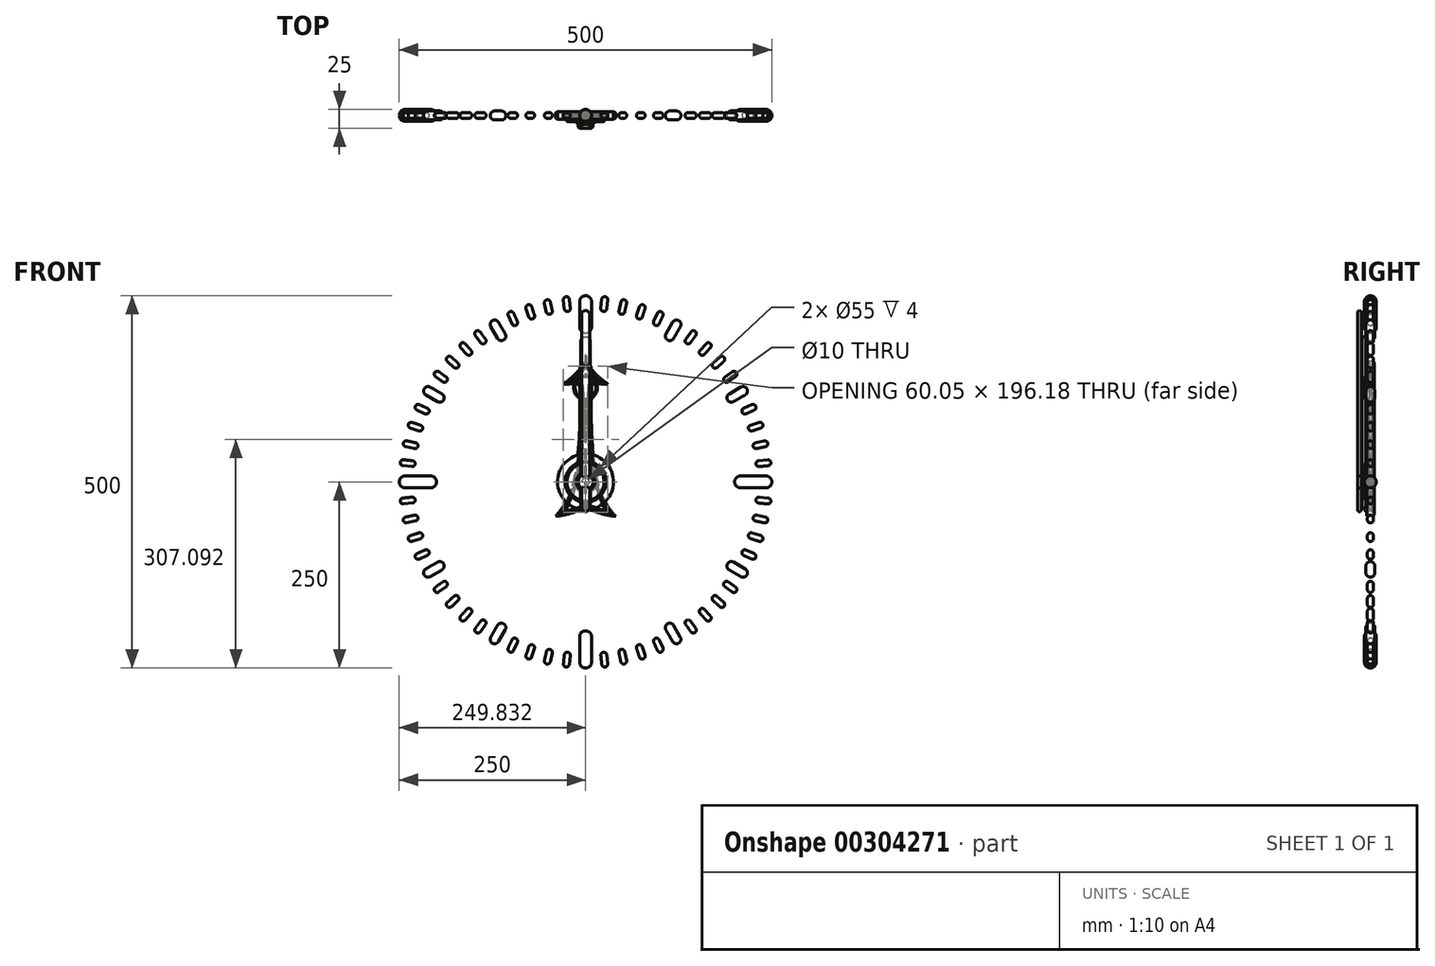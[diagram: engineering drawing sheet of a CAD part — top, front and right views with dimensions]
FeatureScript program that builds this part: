
annotation { "Feature Type Name" : "Feature", "Feature Type Description" : "" }
export const myFeature = defineFeature(function(context is Context, id is Id, definition is map)
    precondition{}
    {
        {
            var Q0;
            Q0=qCreatedBy(makeId("Top.planeOp"),FACE);
            cPlane(context, id + "F0", {"entities" : qUnion([Q0]), "cplaneType" : CPlaneType.OFFSET, "offset" : 250 * mm, "width" : 150 * mm, "height" : 150 * mm});
        }
        {
            var Q0;
            Q0=qCreatedBy(id+"F0.planeOp",FACE);
            var sketch = newSketch(context, id + "F1", { "sketchPlane" : qUnion([Q0])});
            skCircle(sketch, "E0", {"center": v(0, 0) * mm, "radius": 8 * mm});
            skSolve(sketch);
        }
        {
            var Q0;
            Q0 = qSketchRegion(id + "F1", true);
            extrude(context, id + "F2", {"entities" : qUnion([Q0]), "oppositeDirection" : true, "depth" : 50 * mm});
        }
        {
            var Q0;
            Q0=makeQuery(id+"F2.opExtrude","CAP_EDGE",EDGE,{"disambiguationData":[OSD([sQuery(id+"F1.wireOp",EDGE,"E0")])],"isStart":false});
            var Q1;
            Q1=makeQuery(id+"F2.opExtrude","CAP_EDGE",EDGE,{"disambiguationData":[OSD([sQuery(id+"F1.wireOp",EDGE,"E0")])],"isStart":true});
            fillet(context, id + "F3", {"entities" : qUnion([Q0, Q1]), "radius" : 8 * mm, "tangentPropagation" : true, "allowEdgeOverflow" : false});
        }
        {
            var Q0;
            Q0=qCreatedBy(makeId("Top.planeOp"),FACE);
            var sketch = newSketch(context, id + "F4", { "sketchPlane" : qUnion([Q0])});
            skLineSegment(sketch, "E1", {"start": v(0, 0) * mm, "end": v(0, -158.72) * mm});
            skSolve(sketch);
        }
        {
            var Q0;
            Q0=makeQuery(id+"F2.opExtrude","SWEPT_BODY",BODY,{"disambiguationData":[OSD([sQuery(id+"F1.wireOp",EDGE,"E0")])]});
            var Q1;
            Q1=sQuery(id+"F4.wireOp",EDGE,"E1");
            circularPattern(context, id + "F5", {"entities" : qUnion([Q0]), "axis" : qUnion([Q1]), "angle" : 360 * degree, "instanceCount" : 4, "equalSpace" : true});
        }
        {
            var Q0;
            Q0=qCreatedBy(id+"F0.planeOp",FACE);
            var sketch = newSketch(context, id + "F6", { "sketchPlane" : qUnion([Q0])});
            skCircle(sketch, "E2", {"center": v(0, 0) * mm, "radius": 6 * mm});
            skSolve(sketch);
        }
        {
            var Q0;
            Q0 = qSketchRegion(id + "F6", true);
            extrude(context, id + "F7", {"entities" : qUnion([Q0]), "oppositeDirection" : true, "depth" : 30 * mm});
        }
        {
            var Q0;
            Q0=makeQuery(id+"F7.opExtrude","CAP_EDGE",EDGE,{"disambiguationData":[OSD([sQuery(id+"F6.wireOp",EDGE,"E2")])],"isStart":true});
            var Q1;
            Q1=makeQuery(id+"F7.opExtrude","CAP_EDGE",EDGE,{"disambiguationData":[OSD([sQuery(id+"F6.wireOp",EDGE,"E2")])],"isStart":false});
            fillet(context, id + "F8", {"entities" : qUnion([Q0, Q1]), "radius" : 6 * mm, "tangentPropagation" : true, "allowEdgeOverflow" : false});
        }
        {
            var Q0;
            Q0=makeQuery(id+"F7.opExtrude","SWEPT_BODY",BODY,{"disambiguationData":[OSD([sQuery(id+"F6.wireOp",EDGE,"E2")])]});
            var Q1;
            Q1=sQuery(id+"F4.wireOp",EDGE,"E1");
            transform(context, id + "F9", {"entities" : qUnion([Q0]), "transformType" : TransformType.ROTATION, "transformAxis" : qUnion([Q1]), "angle" : 30 * degree, "oppositeDirection" : true, "makeCopy" : true});
        }
        {
            var Q0;
            Q0=makeQuery(id+"F7.opExtrude","SWEPT_BODY",BODY,{"disambiguationData":[OSD([sQuery(id+"F6.wireOp",EDGE,"E2")])]});
            var Q1;
            Q1=sQuery(id+"F4.wireOp",EDGE,"E1");
            transform(context, id + "F10", {"entities" : qUnion([Q0]), "transformType" : TransformType.ROTATION, "transformAxis" : qUnion([Q1]), "angle" : 60 * degree, "oppositeDirection" : true, "makeCopy" : false});
        }
        {
            var Q0;
            Q0=makeQuery(id+"F9.opPattern","COPY",BODY,{"derivedFrom":makeQuery(id+"F7.opExtrude","SWEPT_BODY",BODY,{"disambiguationData":[OSD([sQuery(id+"F6.wireOp",EDGE,"E2")])]}),"instanceName":"1"});
            var Q1;
            Q1=makeQuery(id+"F7.opExtrude","SWEPT_BODY",BODY,{"disambiguationData":[OSD([sQuery(id+"F6.wireOp",EDGE,"E2")])]});
            var Q2;
            Q2=sQuery(id+"F4.wireOp",EDGE,"E1");
            circularPattern(context, id + "F11", {"entities" : qUnion([Q0, Q1]), "axis" : qUnion([Q2]), "angle" : 360 * degree, "instanceCount" : 4, "equalSpace" : true});
        }
        {
            var Q0;
            Q0=qCreatedBy(id+"F0.planeOp",FACE);
            var sketch = newSketch(context, id + "F12", { "sketchPlane" : qUnion([Q0])});
            skCircle(sketch, "E3", {"center": v(0, 0) * mm, "radius": 4 * mm});
            skSolve(sketch);
        }
        {
            var Q0;
            Q0 = qSketchRegion(id + "F12", true);
            extrude(context, id + "F13", {"entities" : qUnion([Q0]), "oppositeDirection" : true, "depth" : 20 * mm});
        }
        {
            var Q0;
            Q0=makeQuery(id+"F13.opExtrude","CAP_EDGE",EDGE,{"disambiguationData":[OSD([sQuery(id+"F12.wireOp",EDGE,"E3")])],"isStart":false});
            var Q1;
            Q1=makeQuery(id+"F13.opExtrude","CAP_EDGE",EDGE,{"disambiguationData":[OSD([sQuery(id+"F12.wireOp",EDGE,"E3")])],"isStart":true});
            fillet(context, id + "F14", {"entities" : qUnion([Q0, Q1]), "radius" : 4 * mm, "tangentPropagation" : true, "allowEdgeOverflow" : false});
        }
        {
            var Q0;
            Q0=makeQuery(id+"F13.opExtrude","SWEPT_BODY",BODY,{"disambiguationData":[OSD([sQuery(id+"F12.wireOp",EDGE,"E3")])]});
            var Q1;
            Q1=sQuery(id+"F4.wireOp",EDGE,"E1");
            transform(context, id + "F15", {"entities" : qUnion([Q0]), "transformType" : TransformType.ROTATION, "transformAxis" : qUnion([Q1]), "angle" : 6 * degree, "oppositeDirection" : true, "makeCopy" : true});
        }
        {
            var Q0;
            Q0=makeQuery(id+"F13.opExtrude","SWEPT_BODY",BODY,{"disambiguationData":[OSD([sQuery(id+"F12.wireOp",EDGE,"E3")])]});
            var Q1;
            Q1=sQuery(id+"F4.wireOp",EDGE,"E1");
            transform(context, id + "F16", {"entities" : qUnion([Q0]), "transformType" : TransformType.ROTATION, "transformAxis" : qUnion([Q1]), "angle" : 12 * degree, "oppositeDirection" : true, "makeCopy" : true});
        }
        {
            var Q0;
            Q0=makeQuery(id+"F13.opExtrude","SWEPT_BODY",BODY,{"disambiguationData":[OSD([sQuery(id+"F12.wireOp",EDGE,"E3")])]});
            var Q1;
            Q1=sQuery(id+"F4.wireOp",EDGE,"E1");
            transform(context, id + "F17", {"entities" : qUnion([Q0]), "transformType" : TransformType.ROTATION, "transformAxis" : qUnion([Q1]), "angle" : 18 * degree, "oppositeDirection" : true, "makeCopy" : true});
        }
        {
            var Q0;
            Q0=makeQuery(id+"F13.opExtrude","SWEPT_BODY",BODY,{"disambiguationData":[OSD([sQuery(id+"F12.wireOp",EDGE,"E3")])]});
            var Q1;
            Q1=sQuery(id+"F4.wireOp",EDGE,"E1");
            transform(context, id + "F18", {"entities" : qUnion([Q0]), "transformType" : TransformType.ROTATION, "transformAxis" : qUnion([Q1]), "angle" : 24 * degree, "oppositeDirection" : true, "makeCopy" : false});
        }
        {
            var Q0;
            Q0=makeQuery(id+"F15.opPattern","COPY",BODY,{"derivedFrom":makeQuery(id+"F13.opExtrude","SWEPT_BODY",BODY,{"disambiguationData":[OSD([sQuery(id+"F12.wireOp",EDGE,"E3")])]}),"instanceName":"1"});
            var Q1;
            Q1=makeQuery(id+"F16.opPattern","COPY",BODY,{"derivedFrom":makeQuery(id+"F13.opExtrude","SWEPT_BODY",BODY,{"disambiguationData":[OSD([sQuery(id+"F12.wireOp",EDGE,"E3")])]}),"instanceName":"1"});
            var Q2;
            Q2=makeQuery(id+"F17.opPattern","COPY",BODY,{"derivedFrom":makeQuery(id+"F13.opExtrude","SWEPT_BODY",BODY,{"disambiguationData":[OSD([sQuery(id+"F12.wireOp",EDGE,"E3")])]}),"instanceName":"1"});
            var Q3;
            Q3=makeQuery(id+"F13.opExtrude","SWEPT_BODY",BODY,{"disambiguationData":[OSD([sQuery(id+"F12.wireOp",EDGE,"E3")])]});
            var Q4;
            Q4=sQuery(id+"F4.wireOp",EDGE,"E1");
            circularPattern(context, id + "F19", {"entities" : qUnion([Q0, Q1, Q2, Q3]), "axis" : qUnion([Q4]), "angle" : 360 * degree, "instanceCount" : 12, "equalSpace" : true});
        }
        {
            var Q0;
            Q0=qCreatedBy(makeId("Front.planeOp"),FACE);
            var sketch = newSketch(context, id + "F20", { "sketchPlane" : qUnion([Q0])});
            skCircle(sketch, "E4", {"center": v(0, 0) * mm, "radius": 15 * mm});
            skLineSegment(sketch, "E5.bottom", {"start": v(7.5, 160) * mm, "end": v(-7.5, 160) * mm});
            skLineSegment(sketch, "E5.top", {"start": v(7.5, -30) * mm, "end": v(-7.5, -30) * mm});
            skLineSegment(sketch, "E5.left", {"start": v(7.5, 160) * mm, "end": v(7.5, -30) * mm});
            skLineSegment(sketch, "E5.right", {"start": v(-7.5, 160) * mm, "end": v(-7.5, -30) * mm});
            skPoint(sketch, "E5.middle", {"position": v(0, 65) * mm});
            skSolve(sketch);
        }
        {
            var Q0;
            Q0 = qSketchRegion(id + "F20", true);
            extrude(context, id + "F21", {"entities" : qUnion([Q0]), "depth" : 5 * mm});
        }
        {
            var Q0;
            Q0=makeQuery(id+"F21.opExtrude","CAP_FACE",FACE,{"disambiguationData":[OSD([sQuery(id+"F20.wireOp",EDGE,"E4"),sQuery(id+"F20.wireOp",EDGE,"E5.bottom"),sQuery(id+"F20.wireOp",EDGE,"E5.top"),sQuery(id+"F20.wireOp",EDGE,"E5.left"),sQuery(id+"F20.wireOp",EDGE,"E5.right")])],"isStart":false});
            cPlane(context, id + "F22", {"entities" : qUnion([Q0]), "cplaneType" : CPlaneType.OFFSET, "offset" : 1 * mm, "width" : 150 * mm, "height" : 150 * mm});
        }
        {
            var Q0;
            Q0=qCreatedBy(id+"F22.planeOp",FACE);
            var sketch = newSketch(context, id + "F23", { "sketchPlane" : qUnion([Q0])});
            skCircle(sketch, "E6", {"center": v(0, 0) * mm, "radius": 12.5 * mm});
            skLineSegment(sketch, "E7.bottom", {"start": v(6.5, -35) * mm, "end": v(-6.5, -35) * mm});
            skLineSegment(sketch, "E7.top", {"start": v(6.5, 195) * mm, "end": v(-6.5, 195) * mm});
            skLineSegment(sketch, "E7.left", {"start": v(6.5, -35) * mm, "end": v(6.5, 195) * mm});
            skLineSegment(sketch, "E7.right", {"start": v(-6.5, -35) * mm, "end": v(-6.5, 195) * mm});
            skPoint(sketch, "E7.middle", {"position": v(0, 80) * mm});
            skSolve(sketch);
        }
        {
            var Q0;
            Q0 = qSketchRegion(id + "F23", true);
            extrude(context, id + "F24", {"entities" : qUnion([Q0]), "depth" : 5 * mm});
        }
        {
            var Q0;
            Q0=makeQuery(id+"F24.opExtrude","CAP_FACE",FACE,{"disambiguationData":[OSD([sQuery(id+"F23.wireOp",EDGE,"E6"),sQuery(id+"F23.wireOp",EDGE,"E7.bottom"),sQuery(id+"F23.wireOp",EDGE,"E7.top"),sQuery(id+"F23.wireOp",EDGE,"E7.left"),sQuery(id+"F23.wireOp",EDGE,"E7.right")])],"isStart":false});
            cPlane(context, id + "F25", {"entities" : qUnion([Q0]), "cplaneType" : CPlaneType.OFFSET, "offset" : 1 * mm, "width" : 150 * mm, "height" : 150 * mm});
        }
        {
            var Q0;
            Q0=qCreatedBy(id+"F25.planeOp",FACE);
            var sketch = newSketch(context, id + "F26", { "sketchPlane" : qUnion([Q0])});
            skCircle(sketch, "E8", {"center": v(0, 0) * mm, "radius": 10 * mm});
            skLineSegment(sketch, "E9.bottom", {"start": v(5.5, -40) * mm, "end": v(-5.5, -40) * mm});
            skLineSegment(sketch, "E9.top", {"start": v(5.5, 230) * mm, "end": v(-5.5, 230) * mm});
            skLineSegment(sketch, "E9.left", {"start": v(5.5, -40) * mm, "end": v(5.5, 230) * mm});
            skLineSegment(sketch, "E9.right", {"start": v(-5.5, -40) * mm, "end": v(-5.5, 230) * mm});
            skPoint(sketch, "E9.middle", {"position": v(0, 95) * mm});
            skSolve(sketch);
        }
        {
            var Q0;
            Q0 = qSketchRegion(id + "F26", true);
            extrude(context, id + "F27", {"entities" : qUnion([Q0]), "depth" : 5 * mm});
        }
        {
            var Q0;
            Q0=qCreatedBy(makeId("Front.planeOp"),FACE);
            var sketch = newSketch(context, id + "F28", { "sketchPlane" : qUnion([Q0])});
            skCircle(sketch, "E10", {"center": v(0, 0) * mm, "radius": 37.5 * mm});
            skCircle(sketch, "E11", {"center": v(0, 0) * mm, "radius": 5 * mm});
            skSolve(sketch);
        }
        {
            var Q0;
            Q0 = qSketchRegion(id + "F28", true);
            extrude(context, id + "F29", {"entities" : qUnion([Q0]), "depth" : 10 * mm, "symmetric" : true});
        }
        {
            var Q0;
            Q0=makeQuery(id+"F29.opExtrude","CAP_FACE",FACE,{"disambiguationData":[OSD([sQuery(id+"F28.wireOp",EDGE,"E10"),sQuery(id+"F28.wireOp",EDGE,"E11")])],"isStart":false});
            var sketch = newSketch(context, id + "F30", { "sketchPlane" : qUnion([Q0])});
            skCircle(sketch, "E12", {"center": v(0, 0) * mm, "radius": 27.5 * mm});
            skCircle(sketch, "E13", {"center": v(0, 0) * mm, "radius": 5 * mm});
            skSolve(sketch);
        }
        {
            var Q0;
            Q0 = qSketchRegion(id + "F30", true);
            extrude(context, id + "F31", {"entities" : qUnion([Q0]), "oppositeDirection" : true, "depth" : 4 * mm});
        }
        {
            var Q0;
            Q0=makeQuery(id+"F31.opExtrude","SWEPT_BODY",BODY,{"disambiguationData":[OSD([sQuery(id+"F30.wireOp",EDGE,"E12"),sQuery(id+"F30.wireOp",EDGE,"E13")])]});
            var Q1;
            Q1=qCreatedBy(makeId("Front.planeOp"),FACE);
            mirror(context, id + "F32", {"entities" : qUnion([Q0]), "mirrorPlane" : qUnion([Q1])});
        }
        {
            var Q0;
            Q0=makeQuery(id+"F31.opExtrude","SWEPT_BODY",BODY,{"disambiguationData":[OSD([sQuery(id+"F30.wireOp",EDGE,"E12"),sQuery(id+"F30.wireOp",EDGE,"E13")])]});
            var Q1;
            Q1=makeQuery(id+"F32.opPattern","COPY",BODY,{"derivedFrom":makeQuery(id+"F31.opExtrude","SWEPT_BODY",BODY,{"disambiguationData":[OSD([sQuery(id+"F30.wireOp",EDGE,"E12"),sQuery(id+"F30.wireOp",EDGE,"E13")])]}),"instanceName":"1"});
            var Q2;
            Q2=makeQuery(id+"F29.opExtrude","SWEPT_BODY",BODY,{"disambiguationData":[OSD([sQuery(id+"F28.wireOp",EDGE,"E10"),sQuery(id+"F28.wireOp",EDGE,"E11")])]});
            booleanBodies(context, id + "F33", {"operationType" : BooleanOperationType.SUBTRACTION, "tools" : qUnion([Q0, Q1]), "targets" : qUnion([Q2])});
        }
        {
            var Q0;
            Q0=qCreatedBy(makeId("Front.planeOp"),FACE);
            var sketch = newSketch(context, id + "F34", { "sketchPlane" : qUnion([Q0])});
            skLineSegment(sketch, "E14", {"start": v(0, 266.38) * mm, "end": v(0, -269.97) * mm, "construction": true});
            skFitSpline(sketch, "E15", {"points": [v(0, -36.62) * mm, v(-40.37, -46.15) * mm], "startDerivative": vector(-46.8, -5.58) * mm, "endDerivative": vector(-74.3, -7.08) * mm});
            skFitSpline(sketch, "E16", {"points": [v(0, 162.63) * mm, v(-29.95, 131.2) * mm], "startDerivative": vector(-29.1, -46) * mm, "endDerivative": vector(-42.46, -30.96) * mm});
            skFitSpline(sketch, "E17", {"points": [v(-29.95, 131.2) * mm, v(-7.93, 120.46) * mm], "startDerivative": vector(71.66, 2.65) * mm, "endDerivative": vector(0.16, -36.44) * mm});
            skFitSpline(sketch, "E18", {"points": [v(-7.93, 120.46) * mm, v(-40.37, -46.15) * mm], "startDerivative": vector(0.4, -90.92) * mm, "endDerivative": vector(-112.63, -107.42) * mm});
            skFitSpline(sketch, "E19.MirrorCS", {"points": [v(0, -36.62) * mm, v(40.37, -46.15) * mm], "startDerivative": vector(46.8, -5.58) * mm, "endDerivative": vector(74.3, -7.08) * mm});
            skFitSpline(sketch, "E20.MirrorCS", {"points": [v(29.95, 131.2) * mm, v(7.93, 120.46) * mm], "startDerivative": vector(-71.66, 2.65) * mm, "endDerivative": vector(-0.16, -36.44) * mm});
            skFitSpline(sketch, "E21.MirrorCS", {"points": [v(7.93, 120.46) * mm, v(40.37, -46.15) * mm], "startDerivative": vector(-0.4, -90.92) * mm, "endDerivative": vector(112.63, -107.42) * mm});
            skFitSpline(sketch, "E22.MirrorCS", {"points": [v(0, 162.63) * mm, v(29.95, 131.2) * mm], "startDerivative": vector(29.1, -46) * mm, "endDerivative": vector(42.46, -30.96) * mm});
            skSolve(sketch);
        }
        {
            var Q0;
            Q0 = qSketchRegion(id + "F34", true);
            extrude(context, id + "F35", {"entities" : qUnion([Q0]), "depth" : 10 * mm, "symmetric" : true});
        }
        {
            var Q0;
            Q0=makeQuery(id+"F35.opExtrude","CAP_FACE",FACE,{"disambiguationData":[OSD([sQuery(id+"F34.wireOp",EDGE,"E15"),sQuery(id+"F34.wireOp",EDGE,"E16"),sQuery(id+"F34.wireOp",EDGE,"E17"),sQuery(id+"F34.wireOp",EDGE,"E18"),sQuery(id+"F34.wireOp",EDGE,"E19.MirrorCS"),sQuery(id+"F34.wireOp",EDGE,"E20.MirrorCS"),sQuery(id+"F34.wireOp",EDGE,"E21.MirrorCS"),sQuery(id+"F34.wireOp",EDGE,"E22.MirrorCS")])],"isStart":false});
            var sketch = newSketch(context, id + "F36", { "sketchPlane" : qUnion([Q0])});
            skFitSpline(sketch, "E23.0", {"points": [v(-30.1, 135.2) * mm, v(-27.12, 135.3) * mm, v(-23.25, 135.47) * mm, v(-19.07, 135.59) * mm, v(-16.36, 135.62) * mm, v(-14.02, 135.56) * mm, v(-11.95, 135.39) * mm, v(-10.36, 135.1) * mm, v(-9.11, 134.7) * mm, v(-8.19, 134.3) * mm, v(-7.29, 133.78) * mm, v(-6.44, 133.1) * mm, v(-5.7, 132.3) * mm, v(-5.12, 131.4) * mm, v(-4.69, 130.5) * mm, v(-4.28, 129.3) * mm, v(-4.03, 127.87) * mm, v(-3.92, 126.2) * mm, v(-3.9, 124.47) * mm, v(-3.92, 122.6) * mm, v(-3.93, 121.21) * mm, v(-3.93, 120.48) * mm]});
            skFitSpline(sketch, "E23.1", {"points": [v(3.38, 160.5) * mm, v(0.92, 156.6) * mm, v(-2.48, 151.6) * mm, v(-6.95, 146) * mm, v(-10.4, 142.2) * mm, v(-14.06, 138.66) * mm, v(-19.38, 134.08) * mm, v(-24.02, 130.57) * mm, v(-27.6, 127.97) * mm]});
            skFitSpline(sketch, "E23.2", {"points": [v(-3.93, 120.48) * mm, v(-3.92, 118.6) * mm, v(-3.87, 114.3) * mm, v(-3.7, 103.68) * mm, v(-3.55, 87.23) * mm, v(-4.03, 64) * mm, v(-5.74, 38.87) * mm, v(-9.24, 13.38) * mm, v(-14.15, -6.89) * mm, v(-19.6, -21.77) * mm, v(-24.53, -32.07) * mm, v(-30.43, -41.31) * mm, v(-35.08, -46.63) * mm, v(-37.6, -49.04) * mm]});
            skFitSpline(sketch, "E23.3", {"points": [v(27.6, 127.97) * mm, v(24.02, 130.57) * mm, v(19.38, 134.08) * mm, v(14.06, 138.66) * mm, v(10.4, 142.2) * mm, v(6.95, 146) * mm, v(2.48, 151.6) * mm, v(-0.92, 156.6) * mm, v(-3.38, 160.5) * mm]});
            skFitSpline(sketch, "E23.4", {"points": [v(-39.78, -42.16) * mm, v(-36.77, -41.88) * mm, v(-31.53, -41.22) * mm, v(-25.59, -40.05) * mm, v(-21.03, -38.8) * mm, v(-17.28, -37.49) * mm, v(-13.73, -36.11) * mm, v(-9.86, -34.74) * mm, v(-5.3, -33.51) * mm, v(-1.6, -32.9) * mm, v(0.47, -32.65) * mm]});
            skFitSpline(sketch, "E23.5", {"points": [v(0.47, -32.65) * mm, v(2.53, -32.9) * mm, v(6.2, -33.5) * mm, v(10.7, -34.71) * mm, v(14.53, -36.08) * mm, v(18.09, -37.45) * mm, v(21.87, -38.77) * mm, v(26.47, -40.04) * mm, v(32.46, -41.21) * mm, v(37.72, -41.88) * mm, v(40.75, -42.16) * mm]});
            skFitSpline(sketch, "E23.6", {"points": [v(37.8, -49.5) * mm, v(35.25, -47.06) * mm, v(30.55, -41.69) * mm, v(24.6, -32.37) * mm, v(19.64, -22) * mm, v(14.17, -7.06) * mm, v(9.25, 13.26) * mm, v(5.74, 38.8) * mm, v(4.04, 63.98) * mm, v(3.55, 87.22) * mm, v(3.7, 103.69) * mm, v(3.87, 114.3) * mm, v(3.92, 118.61) * mm, v(3.93, 120.48) * mm]});
            skFitSpline(sketch, "E23.7", {"points": [v(3.93, 120.48) * mm, v(3.93, 121.21) * mm, v(3.92, 122.6) * mm, v(3.9, 124.47) * mm, v(3.92, 126.2) * mm, v(4.03, 127.87) * mm, v(4.28, 129.3) * mm, v(4.69, 130.5) * mm, v(5.12, 131.4) * mm, v(5.7, 132.3) * mm, v(6.44, 133.1) * mm, v(7.29, 133.78) * mm, v(8.19, 134.3) * mm, v(9.11, 134.7) * mm, v(10.36, 135.1) * mm, v(11.95, 135.39) * mm, v(14.02, 135.56) * mm, v(16.36, 135.62) * mm, v(19.07, 135.59) * mm, v(23.25, 135.47) * mm, v(27.12, 135.3) * mm, v(30.1, 135.2) * mm]});
            skSolve(sketch);
        }
        {
            var Q0;
            Q0 = qSketchRegion(id + "F36", true);
            extrude(context, id + "F37", {"entities" : qUnion([Q0]), "oppositeDirection" : true, "depth" : 3 * mm});
        }
        {
            var Q0;
            Q0=makeQuery(id+"F37.opExtrude","SWEPT_BODY",BODY,{"disambiguationData":[OSD([sQuery(id+"F36.wireOp",EDGE,"cb9f9798-f91a-4ab6-8642-1e6ef36e4919.0.0"),sQuery(id+"F36.wireOp",EDGE,"cb9f9798-f91a-4ab6-8642-1e6ef36e4919.0.1"),sQuery(id+"F36.wireOp",EDGE,"cb9f9798-f91a-4ab6-8642-1e6ef36e4919.0.2"),sQuery(id+"F36.wireOp",EDGE,"cb9f9798-f91a-4ab6-8642-1e6ef36e4919.0.3"),sQuery(id+"F36.wireOp",EDGE,"cb9f9798-f91a-4ab6-8642-1e6ef36e4919.0.4"),sQuery(id+"F36.wireOp",EDGE,"cb9f9798-f91a-4ab6-8642-1e6ef36e4919.0.5"),sQuery(id+"F36.wireOp",EDGE,"cb9f9798-f91a-4ab6-8642-1e6ef36e4919.0.6"),sQuery(id+"F36.wireOp",EDGE,"cb9f9798-f91a-4ab6-8642-1e6ef36e4919.0.7"),sQuery(id+"F36.wireOp",EDGE,"E23.0"),sQuery(id+"F36.wireOp",EDGE,"E23.1"),sQuery(id+"F36.wireOp",EDGE,"E23.2"),sQuery(id+"F36.wireOp",EDGE,"E23.3"),sQuery(id+"F36.wireOp",EDGE,"E23.4"),sQuery(id+"F36.wireOp",EDGE,"E23.5"),sQuery(id+"F36.wireOp",EDGE,"E23.6"),sQuery(id+"F36.wireOp",EDGE,"E23.7")])]});
            var Q1;
            Q1=qCreatedBy(makeId("Front.planeOp"),FACE);
            mirror(context, id + "F38", {"entities" : qUnion([Q0]), "mirrorPlane" : qUnion([Q1])});
        }
        {
            var Q0;
            Q0=makeQuery(id+"F37.opExtrude","SWEPT_BODY",BODY,{"disambiguationData":[OSD([sQuery(id+"F36.wireOp",EDGE,"cb9f9798-f91a-4ab6-8642-1e6ef36e4919.0.0"),sQuery(id+"F36.wireOp",EDGE,"cb9f9798-f91a-4ab6-8642-1e6ef36e4919.0.1"),sQuery(id+"F36.wireOp",EDGE,"cb9f9798-f91a-4ab6-8642-1e6ef36e4919.0.2"),sQuery(id+"F36.wireOp",EDGE,"cb9f9798-f91a-4ab6-8642-1e6ef36e4919.0.3"),sQuery(id+"F36.wireOp",EDGE,"cb9f9798-f91a-4ab6-8642-1e6ef36e4919.0.4"),sQuery(id+"F36.wireOp",EDGE,"cb9f9798-f91a-4ab6-8642-1e6ef36e4919.0.5"),sQuery(id+"F36.wireOp",EDGE,"cb9f9798-f91a-4ab6-8642-1e6ef36e4919.0.6"),sQuery(id+"F36.wireOp",EDGE,"cb9f9798-f91a-4ab6-8642-1e6ef36e4919.0.7"),sQuery(id+"F36.wireOp",EDGE,"E23.0"),sQuery(id+"F36.wireOp",EDGE,"E23.1"),sQuery(id+"F36.wireOp",EDGE,"E23.2"),sQuery(id+"F36.wireOp",EDGE,"E23.3"),sQuery(id+"F36.wireOp",EDGE,"E23.4"),sQuery(id+"F36.wireOp",EDGE,"E23.5"),sQuery(id+"F36.wireOp",EDGE,"E23.6"),sQuery(id+"F36.wireOp",EDGE,"E23.7")])]});
            var Q1;
            Q1=makeQuery(id+"F38.opPattern","COPY",BODY,{"derivedFrom":makeQuery(id+"F37.opExtrude","SWEPT_BODY",BODY,{"disambiguationData":[OSD([sQuery(id+"F36.wireOp",EDGE,"cb9f9798-f91a-4ab6-8642-1e6ef36e4919.0.0"),sQuery(id+"F36.wireOp",EDGE,"cb9f9798-f91a-4ab6-8642-1e6ef36e4919.0.1"),sQuery(id+"F36.wireOp",EDGE,"cb9f9798-f91a-4ab6-8642-1e6ef36e4919.0.2"),sQuery(id+"F36.wireOp",EDGE,"cb9f9798-f91a-4ab6-8642-1e6ef36e4919.0.3"),sQuery(id+"F36.wireOp",EDGE,"cb9f9798-f91a-4ab6-8642-1e6ef36e4919.0.4"),sQuery(id+"F36.wireOp",EDGE,"cb9f9798-f91a-4ab6-8642-1e6ef36e4919.0.5"),sQuery(id+"F36.wireOp",EDGE,"cb9f9798-f91a-4ab6-8642-1e6ef36e4919.0.6"),sQuery(id+"F36.wireOp",EDGE,"cb9f9798-f91a-4ab6-8642-1e6ef36e4919.0.7"),sQuery(id+"F36.wireOp",EDGE,"E23.0"),sQuery(id+"F36.wireOp",EDGE,"E23.1"),sQuery(id+"F36.wireOp",EDGE,"E23.2"),sQuery(id+"F36.wireOp",EDGE,"E23.3"),sQuery(id+"F36.wireOp",EDGE,"E23.4"),sQuery(id+"F36.wireOp",EDGE,"E23.5"),sQuery(id+"F36.wireOp",EDGE,"E23.6"),sQuery(id+"F36.wireOp",EDGE,"E23.7")])]}),"instanceName":"1"});
            var Q2;
            Q2=makeQuery(id+"F35.opExtrude","SWEPT_BODY",BODY,{"disambiguationData":[OSD([sQuery(id+"F34.wireOp",EDGE,"E15"),sQuery(id+"F34.wireOp",EDGE,"E16"),sQuery(id+"F34.wireOp",EDGE,"E17"),sQuery(id+"F34.wireOp",EDGE,"E18"),sQuery(id+"F34.wireOp",EDGE,"E19.MirrorCS"),sQuery(id+"F34.wireOp",EDGE,"E20.MirrorCS"),sQuery(id+"F34.wireOp",EDGE,"E21.MirrorCS"),sQuery(id+"F34.wireOp",EDGE,"E22.MirrorCS")])]});
            booleanBodies(context, id + "F39", {"operationType" : BooleanOperationType.SUBTRACTION, "tools" : qUnion([Q0, Q1]), "targets" : qUnion([Q2])});
        }
        {
            var Q0;
            Q0=makeQuery(id+"F39.opBoolean","COPY",EDGE,{"derivedFrom":makeQuery(id+"F38.opPattern","COPY",EDGE,{"derivedFrom":makeQuery(id+"F37.opExtrude","SWEPT_EDGE",EDGE,{"disambiguationData":[OSD([sQuery(id+"F36.wireOp",EDGE,"E23.4"),sQuery(id+"F36.wireOp",EDGE,"E23.5")])]}),"instanceName":"1"})});
            var Q1;
            Q1=makeQuery(id+"F35.opExtrude","SWEPT_EDGE",EDGE,{"disambiguationData":[OSD([sQuery(id+"F34.wireOp",EDGE,"E15"),sQuery(id+"F34.wireOp",EDGE,"E19.MirrorCS")])]});
            var Q2;
            Q2=makeQuery(id+"F39.opBoolean","COPY",EDGE,{"derivedFrom":makeQuery(id+"F37.opExtrude","SWEPT_EDGE",EDGE,{"disambiguationData":[OSD([sQuery(id+"F36.wireOp",EDGE,"E23.4"),sQuery(id+"F36.wireOp",EDGE,"E23.5")])]})});
            fillet(context, id + "F40", {"entities" : qUnion([Q0, Q1, Q2]), "radius" : 10 * mm, "tangentPropagation" : true, "allowEdgeOverflow" : false});
        }
        {
            var Q0;
            Q0=makeQuery(id+"F39.opBoolean","COPY",EDGE,{"derivedFrom":makeQuery(id+"F37.opExtrude","CAP_EDGE",EDGE,{"disambiguationData":[OSD([sQuery(id+"F36.wireOp",EDGE,"9ae596dd-88c0-4f9c-ab1a-e39f6d769622.5")])],"isStart":true})});
            var Q1;
            Q1=makeQuery(id+"F39.opBoolean","COPY",EDGE,{"derivedFrom":makeQuery(id+"F37.opExtrude","CAP_EDGE",EDGE,{"disambiguationData":[OSD([sQuery(id+"F36.wireOp",EDGE,"9ae596dd-88c0-4f9c-ab1a-e39f6d769622.6")])],"isStart":true})});
            var Q2;
            Q2=makeQuery(id+"F39.opBoolean","COPY",EDGE,{"derivedFrom":makeQuery(id+"F37.opExtrude","CAP_EDGE",EDGE,{"disambiguationData":[OSD([sQuery(id+"F36.wireOp",EDGE,"9ae596dd-88c0-4f9c-ab1a-e39f6d769622.7")])],"isStart":true})});
            var Q3;
            Q3=makeQuery(id+"F39.opBoolean","COPY",EDGE,{"derivedFrom":makeQuery(id+"F37.opExtrude","CAP_EDGE",EDGE,{"disambiguationData":[OSD([sQuery(id+"F36.wireOp",EDGE,"9ae596dd-88c0-4f9c-ab1a-e39f6d769622.3")])],"isStart":true})});
            var Q4;
            Q4=makeQuery(id+"F39.opBoolean","COPY",EDGE,{"derivedFrom":makeQuery(id+"F38.opPattern","COPY",EDGE,{"derivedFrom":makeQuery(id+"F37.opExtrude","CAP_EDGE",EDGE,{"disambiguationData":[OSD([sQuery(id+"F36.wireOp",EDGE,"9ae596dd-88c0-4f9c-ab1a-e39f6d769622.7")])],"isStart":true}),"instanceName":"1"})});
            var Q5;
            Q5=makeQuery(id+"F39.opBoolean","COPY",EDGE,{"derivedFrom":makeQuery(id+"F38.opPattern","COPY",EDGE,{"derivedFrom":makeQuery(id+"F37.opExtrude","CAP_EDGE",EDGE,{"disambiguationData":[OSD([sQuery(id+"F36.wireOp",EDGE,"9ae596dd-88c0-4f9c-ab1a-e39f6d769622.5")])],"isStart":true}),"instanceName":"1"})});
            var Q6;
            Q6=makeQuery(id+"F39.opBoolean","COPY",EDGE,{"derivedFrom":makeQuery(id+"F38.opPattern","COPY",EDGE,{"derivedFrom":makeQuery(id+"F37.opExtrude","CAP_EDGE",EDGE,{"disambiguationData":[OSD([sQuery(id+"F36.wireOp",EDGE,"9ae596dd-88c0-4f9c-ab1a-e39f6d769622.3")])],"isStart":true}),"instanceName":"1"})});
            var Q7;
            Q7=makeQuery(id+"F39.opBoolean","COPY",EDGE,{"derivedFrom":makeQuery(id+"F38.opPattern","COPY",EDGE,{"derivedFrom":makeQuery(id+"F37.opExtrude","CAP_EDGE",EDGE,{"disambiguationData":[OSD([sQuery(id+"F36.wireOp",EDGE,"9ae596dd-88c0-4f9c-ab1a-e39f6d769622.6")])],"isStart":true}),"instanceName":"1"})});
            var Q8;
            Q8=makeQuery(id+"F35.opExtrude","CAP_EDGE",EDGE,{"disambiguationData":[OSD([sQuery(id+"F34.wireOp",EDGE,"E21.MirrorCS")])],"isStart":true});
            var Q9;
            Q9=makeQuery(id+"F35.opExtrude","CAP_EDGE",EDGE,{"disambiguationData":[OSD([sQuery(id+"F34.wireOp",EDGE,"E21.MirrorCS")])],"isStart":false});
            var Q10;
            Q10=makeQuery(id+"F35.opExtrude","CAP_EDGE",EDGE,{"disambiguationData":[OSD([sQuery(id+"F34.wireOp",EDGE,"E18")])],"isStart":true});
            var Q11;
            Q11=makeQuery(id+"F35.opExtrude","CAP_EDGE",EDGE,{"disambiguationData":[OSD([sQuery(id+"F34.wireOp",EDGE,"E18")])],"isStart":false});
            var Q12;
            Q12=makeQuery(id+"F35.opExtrude","CAP_EDGE",EDGE,{"disambiguationData":[OSD([sQuery(id+"F34.wireOp",EDGE,"E15")])],"isStart":true});
            var Q13;
            Q13=makeQuery(id+"F35.opExtrude","CAP_EDGE",EDGE,{"disambiguationData":[OSD([sQuery(id+"F34.wireOp",EDGE,"E19.MirrorCS")])],"isStart":true});
            var Q14;
            Q14=makeQuery(id+"F35.opExtrude","CAP_EDGE",EDGE,{"disambiguationData":[OSD([sQuery(id+"F34.wireOp",EDGE,"E15")])],"isStart":false});
            var Q15;
            Q15=makeQuery(id+"F35.opExtrude","CAP_EDGE",EDGE,{"disambiguationData":[OSD([sQuery(id+"F34.wireOp",EDGE,"E19.MirrorCS")])],"isStart":false});
            var Q16;
            Q16=makeQuery(id+"F35.opExtrude","SWEPT_EDGE",EDGE,{"disambiguationData":[OSD([sQuery(id+"F34.wireOp",EDGE,"E15"),sQuery(id+"F34.wireOp",EDGE,"E19.MirrorCS")])]});
            var Q17;
            Q17=makeQuery(id+"F39.opBoolean","COPY",EDGE,{"derivedFrom":makeQuery(id+"F38.opPattern","COPY",EDGE,{"derivedFrom":makeQuery(id+"F37.opExtrude","SWEPT_EDGE",EDGE,{"disambiguationData":[OSD([sQuery(id+"F36.wireOp",EDGE,"9ae596dd-88c0-4f9c-ab1a-e39f6d769622.6"),sQuery(id+"F36.wireOp",EDGE,"9ae596dd-88c0-4f9c-ab1a-e39f6d769622.7")])]}),"instanceName":"1"})});
            var Q18;
            Q18=makeQuery(id+"F35.opExtrude","CAP_EDGE",EDGE,{"disambiguationData":[OSD([sQuery(id+"F34.wireOp",EDGE,"E16")])],"isStart":true});
            var Q19;
            Q19=makeQuery(id+"F35.opExtrude","CAP_EDGE",EDGE,{"disambiguationData":[OSD([sQuery(id+"F34.wireOp",EDGE,"E22.MirrorCS")])],"isStart":true});
            var Q20;
            Q20=makeQuery(id+"F39.opBoolean","COPY",EDGE,{"derivedFrom":makeQuery(id+"F38.opPattern","COPY",EDGE,{"derivedFrom":makeQuery(id+"F37.opExtrude","CAP_EDGE",EDGE,{"disambiguationData":[OSD([sQuery(id+"F36.wireOp",EDGE,"9ae596dd-88c0-4f9c-ab1a-e39f6d769622.0")])],"isStart":true}),"instanceName":"1"})});
            var Q21;
            Q21=makeQuery(id+"F39.opBoolean","COPY",EDGE,{"derivedFrom":makeQuery(id+"F38.opPattern","COPY",EDGE,{"derivedFrom":makeQuery(id+"F37.opExtrude","CAP_EDGE",EDGE,{"disambiguationData":[OSD([sQuery(id+"F36.wireOp",EDGE,"9ae596dd-88c0-4f9c-ab1a-e39f6d769622.2")])],"isStart":true}),"instanceName":"1"})});
            var Q22;
            Q22=makeQuery(id+"F35.opExtrude","CAP_EDGE",EDGE,{"disambiguationData":[OSD([sQuery(id+"F34.wireOp",EDGE,"E16")])],"isStart":false});
            var Q23;
            Q23=makeQuery(id+"F39.opBoolean","COPY",EDGE,{"derivedFrom":makeQuery(id+"F37.opExtrude","CAP_EDGE",EDGE,{"disambiguationData":[OSD([sQuery(id+"F36.wireOp",EDGE,"9ae596dd-88c0-4f9c-ab1a-e39f6d769622.2")])],"isStart":true})});
            var Q24;
            Q24=makeQuery(id+"F39.opBoolean","COPY",EDGE,{"derivedFrom":makeQuery(id+"F37.opExtrude","CAP_EDGE",EDGE,{"disambiguationData":[OSD([sQuery(id+"F36.wireOp",EDGE,"9ae596dd-88c0-4f9c-ab1a-e39f6d769622.0")])],"isStart":true})});
            var Q25;
            Q25=makeQuery(id+"F35.opExtrude","CAP_EDGE",EDGE,{"disambiguationData":[OSD([sQuery(id+"F34.wireOp",EDGE,"E22.MirrorCS")])],"isStart":false});
            var Q26;
            Q26=makeQuery(id+"F35.opExtrude","CAP_EDGE",EDGE,{"disambiguationData":[OSD([sQuery(id+"F34.wireOp",EDGE,"E17")])],"isStart":false});
            fillet(context, id + "F41", {"entities" : qUnion([Q0, Q1, Q2, Q3, Q4, Q5, Q6, Q7, Q8, Q9, Q10, Q11, Q12, Q13, Q14, Q15, Q16, Q17, Q18, Q19, Q20, Q21, Q22, Q23, Q24, Q25, Q26]), "radius" : 2 * mm, "tangentPropagation" : true, "allowEdgeOverflow" : false});
        }
        {
            var Q0;
            Q0=makeQuery(id+"F39.opBoolean","COPY",EDGE,{"derivedFrom":makeQuery(id+"F37.opExtrude","CAP_EDGE",EDGE,{"disambiguationData":[OSD([sQuery(id+"F36.wireOp",EDGE,"E23.1")])],"isStart":true})});
            var Q1;
            Q1=makeQuery(id+"F39.opBoolean","COPY",EDGE,{"derivedFrom":makeQuery(id+"F37.opExtrude","CAP_EDGE",EDGE,{"disambiguationData":[OSD([sQuery(id+"F36.wireOp",EDGE,"E23.1")])],"isStart":false})});
            var Q2;
            Q2=makeQuery(id+"F39.opBoolean","COPY",EDGE,{"derivedFrom":makeQuery(id+"F37.opExtrude","CAP_EDGE",EDGE,{"disambiguationData":[OSD([sQuery(id+"F36.wireOp",EDGE,"E23.3")])],"isStart":false})});
            var Q3;
            Q3=makeQuery(id+"F39.opBoolean","COPY",EDGE,{"derivedFrom":makeQuery(id+"F37.opExtrude","CAP_EDGE",EDGE,{"disambiguationData":[OSD([sQuery(id+"F36.wireOp",EDGE,"E23.3")])],"isStart":true})});
            var Q4;
            Q4=makeQuery(id+"F39.opBoolean","COPY",EDGE,{"derivedFrom":makeQuery(id+"F37.opExtrude","CAP_EDGE",EDGE,{"disambiguationData":[OSD([sQuery(id+"F36.wireOp",EDGE,"E23.7")])],"isStart":false})});
            var Q5;
            Q5=makeQuery(id+"F39.opBoolean","COPY",EDGE,{"derivedFrom":makeQuery(id+"F37.opExtrude","CAP_EDGE",EDGE,{"disambiguationData":[OSD([sQuery(id+"F36.wireOp",EDGE,"E23.7")])],"isStart":true})});
            var Q6;
            Q6=makeQuery(id+"F39.opBoolean","COPY",EDGE,{"derivedFrom":makeQuery(id+"F37.opExtrude","CAP_EDGE",EDGE,{"disambiguationData":[OSD([sQuery(id+"F36.wireOp",EDGE,"E23.0")])],"isStart":true})});
            var Q7;
            Q7=makeQuery(id+"F39.opBoolean","COPY",EDGE,{"derivedFrom":makeQuery(id+"F37.opExtrude","CAP_EDGE",EDGE,{"disambiguationData":[OSD([sQuery(id+"F36.wireOp",EDGE,"E23.0")])],"isStart":false})});
            var Q8;
            Q8=makeQuery(id+"F39.opBoolean","COPY",EDGE,{"derivedFrom":makeQuery(id+"F37.opExtrude","CAP_EDGE",EDGE,{"disambiguationData":[OSD([sQuery(id+"F36.wireOp",EDGE,"E23.4")])],"isStart":false})});
            var Q9;
            Q9=makeQuery(id+"F39.opBoolean","COPY",EDGE,{"derivedFrom":makeQuery(id+"F37.opExtrude","CAP_EDGE",EDGE,{"disambiguationData":[OSD([sQuery(id+"F36.wireOp",EDGE,"E23.5")])],"isStart":false})});
            var Q10;
            Q10=makeQuery(id+"F39.opBoolean","COPY",EDGE,{"derivedFrom":makeQuery(id+"F37.opExtrude","CAP_EDGE",EDGE,{"disambiguationData":[OSD([sQuery(id+"F36.wireOp",EDGE,"E23.5")])],"isStart":true})});
            var Q11;
            Q11=makeQuery(id+"F39.opBoolean","COPY",EDGE,{"derivedFrom":makeQuery(id+"F37.opExtrude","CAP_EDGE",EDGE,{"disambiguationData":[OSD([sQuery(id+"F36.wireOp",EDGE,"E23.4")])],"isStart":true})});
            var Q12;
            Q12=makeQuery(id+"F39.opBoolean","COPY",EDGE,{"derivedFrom":makeQuery(id+"F38.opPattern","COPY",EDGE,{"derivedFrom":makeQuery(id+"F37.opExtrude","CAP_EDGE",EDGE,{"disambiguationData":[OSD([sQuery(id+"F36.wireOp",EDGE,"E23.3")])],"isStart":false}),"instanceName":"1"})});
            var Q13;
            Q13=makeQuery(id+"F39.opBoolean","COPY",EDGE,{"derivedFrom":makeQuery(id+"F38.opPattern","COPY",EDGE,{"derivedFrom":makeQuery(id+"F37.opExtrude","CAP_EDGE",EDGE,{"disambiguationData":[OSD([sQuery(id+"F36.wireOp",EDGE,"E23.3")])],"isStart":true}),"instanceName":"1"})});
            var Q14;
            Q14=makeQuery(id+"F39.opBoolean","COPY",EDGE,{"derivedFrom":makeQuery(id+"F38.opPattern","COPY",EDGE,{"derivedFrom":makeQuery(id+"F37.opExtrude","CAP_EDGE",EDGE,{"disambiguationData":[OSD([sQuery(id+"F36.wireOp",EDGE,"E23.1")])],"isStart":false}),"instanceName":"1"})});
            var Q15;
            Q15=makeQuery(id+"F39.opBoolean","COPY",EDGE,{"derivedFrom":makeQuery(id+"F38.opPattern","COPY",EDGE,{"derivedFrom":makeQuery(id+"F37.opExtrude","CAP_EDGE",EDGE,{"disambiguationData":[OSD([sQuery(id+"F36.wireOp",EDGE,"E23.1")])],"isStart":true}),"instanceName":"1"})});
            var Q16;
            Q16=makeQuery(id+"F39.opBoolean","COPY",EDGE,{"derivedFrom":makeQuery(id+"F38.opPattern","COPY",EDGE,{"derivedFrom":makeQuery(id+"F37.opExtrude","CAP_EDGE",EDGE,{"disambiguationData":[OSD([sQuery(id+"F36.wireOp",EDGE,"E23.7")])],"isStart":true}),"instanceName":"1"})});
            var Q17;
            Q17=makeQuery(id+"F39.opBoolean","COPY",EDGE,{"derivedFrom":makeQuery(id+"F38.opPattern","COPY",EDGE,{"derivedFrom":makeQuery(id+"F37.opExtrude","CAP_EDGE",EDGE,{"disambiguationData":[OSD([sQuery(id+"F36.wireOp",EDGE,"E23.7")])],"isStart":false}),"instanceName":"1"})});
            var Q18;
            Q18=makeQuery(id+"F39.opBoolean","COPY",EDGE,{"derivedFrom":makeQuery(id+"F38.opPattern","COPY",EDGE,{"derivedFrom":makeQuery(id+"F37.opExtrude","CAP_EDGE",EDGE,{"disambiguationData":[OSD([sQuery(id+"F36.wireOp",EDGE,"E23.0")])],"isStart":false}),"instanceName":"1"})});
            var Q19;
            Q19=makeQuery(id+"F39.opBoolean","COPY",EDGE,{"derivedFrom":makeQuery(id+"F38.opPattern","COPY",EDGE,{"derivedFrom":makeQuery(id+"F37.opExtrude","CAP_EDGE",EDGE,{"disambiguationData":[OSD([sQuery(id+"F36.wireOp",EDGE,"E23.0")])],"isStart":true}),"instanceName":"1"})});
            var Q20;
            Q20=makeQuery(id+"F39.opBoolean","COPY",EDGE,{"derivedFrom":makeQuery(id+"F38.opPattern","COPY",EDGE,{"derivedFrom":makeQuery(id+"F37.opExtrude","CAP_EDGE",EDGE,{"disambiguationData":[OSD([sQuery(id+"F36.wireOp",EDGE,"E23.5")])],"isStart":false}),"instanceName":"1"})});
            var Q21;
            Q21=makeQuery(id+"F39.opBoolean","COPY",EDGE,{"derivedFrom":makeQuery(id+"F38.opPattern","COPY",EDGE,{"derivedFrom":makeQuery(id+"F37.opExtrude","CAP_EDGE",EDGE,{"disambiguationData":[OSD([sQuery(id+"F36.wireOp",EDGE,"E23.5")])],"isStart":true}),"instanceName":"1"})});
            var Q22;
            Q22=makeQuery(id+"F39.opBoolean","COPY",EDGE,{"derivedFrom":makeQuery(id+"F38.opPattern","COPY",EDGE,{"derivedFrom":makeQuery(id+"F37.opExtrude","CAP_EDGE",EDGE,{"disambiguationData":[OSD([sQuery(id+"F36.wireOp",EDGE,"E23.4")])],"isStart":false}),"instanceName":"1"})});
            var Q23;
            Q23=makeQuery(id+"F39.opBoolean","COPY",EDGE,{"derivedFrom":makeQuery(id+"F38.opPattern","COPY",EDGE,{"derivedFrom":makeQuery(id+"F37.opExtrude","CAP_EDGE",EDGE,{"disambiguationData":[OSD([sQuery(id+"F36.wireOp",EDGE,"E23.4")])],"isStart":true}),"instanceName":"1"})});
            fillet(context, id + "F42", {"entities" : qUnion([Q0, Q1, Q2, Q3, Q4, Q5, Q6, Q7, Q8, Q9, Q10, Q11, Q12, Q13, Q14, Q15, Q16, Q17, Q18, Q19, Q20, Q21, Q22, Q23]), "radius" : 1 * mm, "tangentPropagation" : true, "allowEdgeOverflow" : false});
        }
        {
            var Q0;
            Q0=qCreatedBy(id+"F22.planeOp",FACE);
            var sketch = newSketch(context, id + "F43", { "sketchPlane" : qUnion([Q0])});
            skLineSegment(sketch, "E24", {"start": v(0, 310.17) * mm, "end": v(0, -199.61) * mm, "construction": true});
            skCircle(sketch, "E25", {"center": v(0, 0) * mm, "radius": 25 * mm});
            skSolve(sketch);
        }
        {
            var Q0;
            Q0 = qSketchRegion(id + "F43", true);
            extrude(context, id + "F44", {"entities" : qUnion([Q0]), "depth" : 5 * mm, "symmetric" : true});
        }
        {
            var Q0;
            Q0=qCreatedBy(id+"F22.planeOp",FACE);
            var sketch = newSketch(context, id + "F45", { "sketchPlane" : qUnion([Q0])});
            skLineSegment(sketch, "E26", {"start": v(0, 111.2) * mm, "end": v(0, -40) * mm});
            skCircle(sketch, "E27", {"center": v(0, 126.2) * mm, "radius": 15 * mm});
            skLineSegment(sketch, "E28", {"start": v(0, 141.2) * mm, "end": v(0, 170) * mm});
            skSolve(sketch);
        }
        {
            var Q0;
            Q0=sQuery(id+"F45.wireOp",EDGE,"E28");
            var Q1;
            Q1=sQuery(id+"F45.wireOp",VERTEX,"E28.end");
            cPlane(context, id + "F46", {"entities" : qUnion([Q0, Q1]), "cplaneType" : CPlaneType.LINE_POINT, "offset" : 25 * mm, "width" : 150 * mm, "height" : 150 * mm});
        }
        {
            var Q0;
            Q0=qCreatedBy(id+"F46.planeOp",FACE);
            var sketch = newSketch(context, id + "F47", { "sketchPlane" : qUnion([Q0])});
            skCircle(sketch, "E29", {"center": v(0, -6) * mm, "radius": 1 * mm});
            skSolve(sketch);
        }
        {
            var Q0;
            Q0=makeQuery(id+"F47.imprint","IMPRINT",FACE,{"disambiguationData":[TD([[makeQuery(id+"F47.imprint","IMPRINT",EDGE,{"derivedFrom":sQuery(id+"F47.wireOp",EDGE,"E29")}),1.0]])]});
            var Q1;
            Q1=sQuery(id+"F45.wireOp",EDGE,"E28");
            sweep(context, id + "F48", {"profiles" : qUnion([Q0]), "path" : qUnion([Q1])});
        }
        {
            var Q0;
            Q0=sQuery(id+"F45.wireOp",VERTEX,"E26.end");
            var Q1;
            Q1=sQuery(id+"F45.wireOp",EDGE,"E26");
            cPlane(context, id + "F49", {"entities" : qUnion([Q0, Q1]), "cplaneType" : CPlaneType.LINE_POINT, "offset" : 25 * mm, "width" : 150 * mm, "height" : 150 * mm});
        }
        {
            var Q0;
            Q0=qCreatedBy(id+"F49.planeOp",FACE);
            var sketch = newSketch(context, id + "F50", { "sketchPlane" : qUnion([Q0])});
            skCircle(sketch, "E30", {"center": v(0, 6) * mm, "radius": 1 * mm});
            skSolve(sketch);
        }
        {
            var Q0;
            Q0=makeQuery(id+"F50.imprint","IMPRINT",FACE,{"disambiguationData":[TD([[makeQuery(id+"F50.imprint","IMPRINT",EDGE,{"derivedFrom":sQuery(id+"F50.wireOp",EDGE,"E30")}),1.0]])]});
            var Q1;
            Q1=sQuery(id+"F45.wireOp",EDGE,"E26");
            sweep(context, id + "F51", {"profiles" : qUnion([Q0]), "path" : qUnion([Q1])});
        }
        {
            var Q0;
            Q0=qCreatedBy(id+"F22.planeOp",FACE);
            var sketch = newSketch(context, id + "F52", { "sketchPlane" : qUnion([Q0])});
            skCircle(sketch, "E31", {"center": v(0, 126.2) * mm, "radius": 16 * mm});
            skCircle(sketch, "E32", {"center": v(0, 126.2) * mm, "radius": 14 * mm});
            skSolve(sketch);
        }
        {
            var Q0;
            Q0 = qSketchRegion(id + "F52", true);
            extrude(context, id + "F53", {"entities" : qUnion([Q0]), "depth" : 2 * mm, "symmetric" : true});
        }
        {
            var Q0;
            Q0=makeQuery(id+"F53.opExtrude","CAP_EDGE",EDGE,{"disambiguationData":[OSD([sQuery(id+"F52.wireOp",EDGE,"E31")])],"isStart":false});
            var Q1;
            Q1=makeQuery(id+"F53.opExtrude","CAP_EDGE",EDGE,{"disambiguationData":[OSD([sQuery(id+"F52.wireOp",EDGE,"E32")])],"isStart":false});
            var Q2;
            Q2=makeQuery(id+"F53.opExtrude","CAP_EDGE",EDGE,{"disambiguationData":[OSD([sQuery(id+"F52.wireOp",EDGE,"E31")])],"isStart":true});
            var Q3;
            Q3=makeQuery(id+"F53.opExtrude","CAP_EDGE",EDGE,{"disambiguationData":[OSD([sQuery(id+"F52.wireOp",EDGE,"E32")])],"isStart":true});
            fillet(context, id + "F54", {"entities" : qUnion([Q0, Q1, Q2, Q3]), "radius" : 1 * mm, "tangentPropagation" : true, "allowEdgeOverflow" : false});
        }
        {
            var Q0;
            Q0=makeQuery(id+"F48.opSweep","CAP_EDGE",EDGE,{"disambiguationData":[OSD([sQuery(id+"F45.wireOp",VERTEX,"E28.end"),sQuery(id+"F47.wireOp",EDGE,"E29")])],"isStart":true});
            var Q1;
            Q1=makeQuery(id+"F51.opSweep","CAP_EDGE",EDGE,{"disambiguationData":[OSD([sQuery(id+"F45.wireOp",VERTEX,"E26.end"),sQuery(id+"F50.wireOp",EDGE,"E30")])],"isStart":true});
            var Q2;
            Q2=makeQuery(id+"F44.opExtrude","CAP_EDGE",EDGE,{"disambiguationData":[OSD([sQuery(id+"F43.wireOp",EDGE,"E25")])],"isStart":false});
            var Q3;
            Q3=makeQuery(id+"F44.opExtrude","CAP_EDGE",EDGE,{"disambiguationData":[OSD([sQuery(id+"F43.wireOp",EDGE,"E25")])],"isStart":true});
            fillet(context, id + "F55", {"entities" : qUnion([Q0, Q1, Q2, Q3]), "radius" : 1 * mm, "tangentPropagation" : true, "allowEdgeOverflow" : false});
        }
        {
            var Q0;
            Q0=makeQuery(id+"F21.opExtrude","SWEPT_EDGE",EDGE,{"disambiguationData":[OSD([sQuery(id+"F20.wireOp",EDGE,"E5.top"),sQuery(id+"F20.wireOp",EDGE,"E5.right")])]});
            var Q1;
            Q1=makeQuery(id+"F21.opExtrude","SWEPT_EDGE",EDGE,{"disambiguationData":[OSD([sQuery(id+"F20.wireOp",EDGE,"E5.top"),sQuery(id+"F20.wireOp",EDGE,"E5.left")])]});
            var Q2;
            Q2=makeQuery(id+"F21.opExtrude","SWEPT_EDGE",EDGE,{"disambiguationData":[OSD([sQuery(id+"F20.wireOp",EDGE,"E5.bottom"),sQuery(id+"F20.wireOp",EDGE,"E5.left")])]});
            var Q3;
            Q3=makeQuery(id+"F21.opExtrude","SWEPT_EDGE",EDGE,{"disambiguationData":[OSD([sQuery(id+"F20.wireOp",EDGE,"E5.bottom"),sQuery(id+"F20.wireOp",EDGE,"E5.right")])]});
            fillet(context, id + "F56", {"entities" : qUnion([Q0, Q1, Q2, Q3]), "radius" : 7.5 * mm, "tangentPropagation" : true, "allowEdgeOverflow" : false});
        }
        {
            var Q0;
            {var subQ0=sQuery(id+"F20.wireOp",EDGE,"E5.right");var subQ1=sQuery(id+"F20.wireOp",EDGE,"E4");Q0=makeQuery(id+"F21.opExtrude","CAP_EDGE",EDGE,{"disambiguationData":[OSD([subQ1]),TDD([makeQuery(id+"F20.imprint","IMPRINT",EDGE,{"disambiguationData":[TD([[makeQuery(id+"F20.imprint","INTERSECT",VERTEX,{"disambiguationData":[OD(0.0)],"derivedFrom":[subQ1,subQ0]}),-1.0]])],"derivedFrom":subQ1})])],"isStart":false});}
            var Q1;
            {var subQ0=sQuery(id+"F20.wireOp",EDGE,"E5.right");Q1=makeQuery(id+"F21.opExtrude","CAP_EDGE",EDGE,{"disambiguationData":[OSD([subQ0]),TDD([makeQuery(id+"F20.imprint","IMPRINT",EDGE,{"disambiguationData":[TD([[makeQuery(id+"F20.imprint","INTERSECT",VERTEX,{"derivedFrom":[sQuery(id+"F20.wireOp",EDGE,"E5.top"),subQ0]}),1.0]])],"derivedFrom":subQ0})])],"isStart":false});}
            var Q2;
            {var subQ0=sQuery(id+"F20.wireOp",EDGE,"E5.left");var subQ1=sQuery(id+"F20.wireOp",EDGE,"E4");Q2=makeQuery(id+"F21.opExtrude","CAP_EDGE",EDGE,{"disambiguationData":[OSD([subQ1]),TDD([makeQuery(id+"F20.imprint","IMPRINT",EDGE,{"disambiguationData":[TD([[makeQuery(id+"F20.imprint","INTERSECT",VERTEX,{"disambiguationData":[OD(0.0)],"derivedFrom":[subQ1,subQ0]}),1.0]])],"derivedFrom":subQ1})])],"isStart":true});}
            var Q3;
            {var subQ0=sQuery(id+"F20.wireOp",EDGE,"E5.left");Q3=makeQuery(id+"F21.opExtrude","CAP_EDGE",EDGE,{"disambiguationData":[OSD([subQ0]),TDD([makeQuery(id+"F20.imprint","IMPRINT",EDGE,{"disambiguationData":[TD([[makeQuery(id+"F20.imprint","INTERSECT",VERTEX,{"derivedFrom":[sQuery(id+"F20.wireOp",EDGE,"E5.bottom"),subQ0]}),-1.0]])],"derivedFrom":subQ0})])],"isStart":false});}
            var Q4;
            Q4=makeQuery(id+"F21.opExtrude","CAP_FACE",FACE,{"disambiguationData":[OSD([sQuery(id+"F20.wireOp",EDGE,"E4"),sQuery(id+"F20.wireOp",EDGE,"E5.bottom"),sQuery(id+"F20.wireOp",EDGE,"E5.top"),sQuery(id+"F20.wireOp",EDGE,"E5.left"),sQuery(id+"F20.wireOp",EDGE,"E5.right"),sQuery(id+"F20.wireOp",EDGE,"5G3UWPod-W6R7-sLE7-Ks05-odvMs3h46zt1")])],"isStart":false});
            var Q5;
            Q5=makeQuery(id+"F21.opExtrude","CAP_FACE",FACE,{"disambiguationData":[OSD([sQuery(id+"F20.wireOp",EDGE,"E4"),sQuery(id+"F20.wireOp",EDGE,"E5.bottom"),sQuery(id+"F20.wireOp",EDGE,"E5.top"),sQuery(id+"F20.wireOp",EDGE,"E5.left"),sQuery(id+"F20.wireOp",EDGE,"E5.right"),sQuery(id+"F20.wireOp",EDGE,"5G3UWPod-W6R7-sLE7-Ks05-odvMs3h46zt1")])],"isStart":true});
            fillet(context, id + "F57", {"entities" : qUnion([Q0, Q1, Q2, Q3, Q4, Q5]), "radius" : 2.5 * mm, "tangentPropagation" : true, "allowEdgeOverflow" : false});
        }
        {
            var Q0;
            Q0=makeQuery(id+"F24.opExtrude","SWEPT_EDGE",EDGE,{"disambiguationData":[OSD([sQuery(id+"F23.wireOp",EDGE,"E7.bottom"),sQuery(id+"F23.wireOp",EDGE,"E7.right")])]});
            var Q1;
            Q1=makeQuery(id+"F24.opExtrude","SWEPT_EDGE",EDGE,{"disambiguationData":[OSD([sQuery(id+"F23.wireOp",EDGE,"E7.bottom"),sQuery(id+"F23.wireOp",EDGE,"E7.left")])]});
            var Q2;
            Q2=makeQuery(id+"F24.opExtrude","SWEPT_EDGE",EDGE,{"disambiguationData":[OSD([sQuery(id+"F23.wireOp",EDGE,"E7.top"),sQuery(id+"F23.wireOp",EDGE,"E7.left")])]});
            var Q3;
            Q3=makeQuery(id+"F24.opExtrude","SWEPT_EDGE",EDGE,{"disambiguationData":[OSD([sQuery(id+"F23.wireOp",EDGE,"E7.top"),sQuery(id+"F23.wireOp",EDGE,"E7.right")])]});
            fillet(context, id + "F58", {"entities" : qUnion([Q0, Q1, Q2, Q3]), "radius" : 6.5 * mm, "tangentPropagation" : true, "allowEdgeOverflow" : false});
        }
        {
            var Q0;
            Q0=makeQuery(id+"F24.opExtrude","CAP_FACE",FACE,{"disambiguationData":[OSD([sQuery(id+"F23.wireOp",EDGE,"E6"),sQuery(id+"F23.wireOp",EDGE,"E7.bottom"),sQuery(id+"F23.wireOp",EDGE,"E7.top"),sQuery(id+"F23.wireOp",EDGE,"E7.left"),sQuery(id+"F23.wireOp",EDGE,"E7.right")])],"isStart":false});
            var Q1;
            Q1=makeQuery(id+"F24.opExtrude","CAP_FACE",FACE,{"disambiguationData":[OSD([sQuery(id+"F23.wireOp",EDGE,"E6"),sQuery(id+"F23.wireOp",EDGE,"E7.bottom"),sQuery(id+"F23.wireOp",EDGE,"E7.top"),sQuery(id+"F23.wireOp",EDGE,"E7.left"),sQuery(id+"F23.wireOp",EDGE,"E7.right")])],"isStart":true});
            fillet(context, id + "F59", {"entities" : qUnion([Q0, Q1]), "radius" : 2.5 * mm, "tangentPropagation" : true, "allowEdgeOverflow" : false});
        }
        {
            var Q0;
            Q0=makeQuery(id+"F27.opExtrude","SWEPT_EDGE",EDGE,{"disambiguationData":[OSD([sQuery(id+"F26.wireOp",EDGE,"E9.top"),sQuery(id+"F26.wireOp",EDGE,"E9.left")])]});
            var Q1;
            Q1=makeQuery(id+"F27.opExtrude","SWEPT_EDGE",EDGE,{"disambiguationData":[OSD([sQuery(id+"F26.wireOp",EDGE,"E9.top"),sQuery(id+"F26.wireOp",EDGE,"E9.right")])]});
            var Q2;
            Q2=makeQuery(id+"F27.opExtrude","SWEPT_EDGE",EDGE,{"disambiguationData":[OSD([sQuery(id+"F26.wireOp",EDGE,"E9.bottom"),sQuery(id+"F26.wireOp",EDGE,"E9.right")])]});
            var Q3;
            Q3=makeQuery(id+"F27.opExtrude","SWEPT_EDGE",EDGE,{"disambiguationData":[OSD([sQuery(id+"F26.wireOp",EDGE,"E9.bottom"),sQuery(id+"F26.wireOp",EDGE,"E9.left")])]});
            fillet(context, id + "F60", {"entities" : qUnion([Q0, Q1, Q2, Q3]), "radius" : 5.5 * mm, "tangentPropagation" : true, "allowEdgeOverflow" : false});
        }
        {
            var Q0;
            Q0=makeQuery(id+"F27.opExtrude","CAP_FACE",FACE,{"disambiguationData":[OSD([sQuery(id+"F26.wireOp",EDGE,"E8"),sQuery(id+"F26.wireOp",EDGE,"E9.bottom"),sQuery(id+"F26.wireOp",EDGE,"E9.top"),sQuery(id+"F26.wireOp",EDGE,"E9.left"),sQuery(id+"F26.wireOp",EDGE,"E9.right")])],"isStart":false});
            var Q1;
            Q1=makeQuery(id+"F27.opExtrude","CAP_FACE",FACE,{"disambiguationData":[OSD([sQuery(id+"F26.wireOp",EDGE,"E8"),sQuery(id+"F26.wireOp",EDGE,"E9.bottom"),sQuery(id+"F26.wireOp",EDGE,"E9.top"),sQuery(id+"F26.wireOp",EDGE,"E9.left"),sQuery(id+"F26.wireOp",EDGE,"E9.right")])],"isStart":true});
            fillet(context, id + "F61", {"entities" : qUnion([Q0, Q1]), "radius" : 2.5 * mm, "tangentPropagation" : true, "allowEdgeOverflow" : false});
        }
    });
